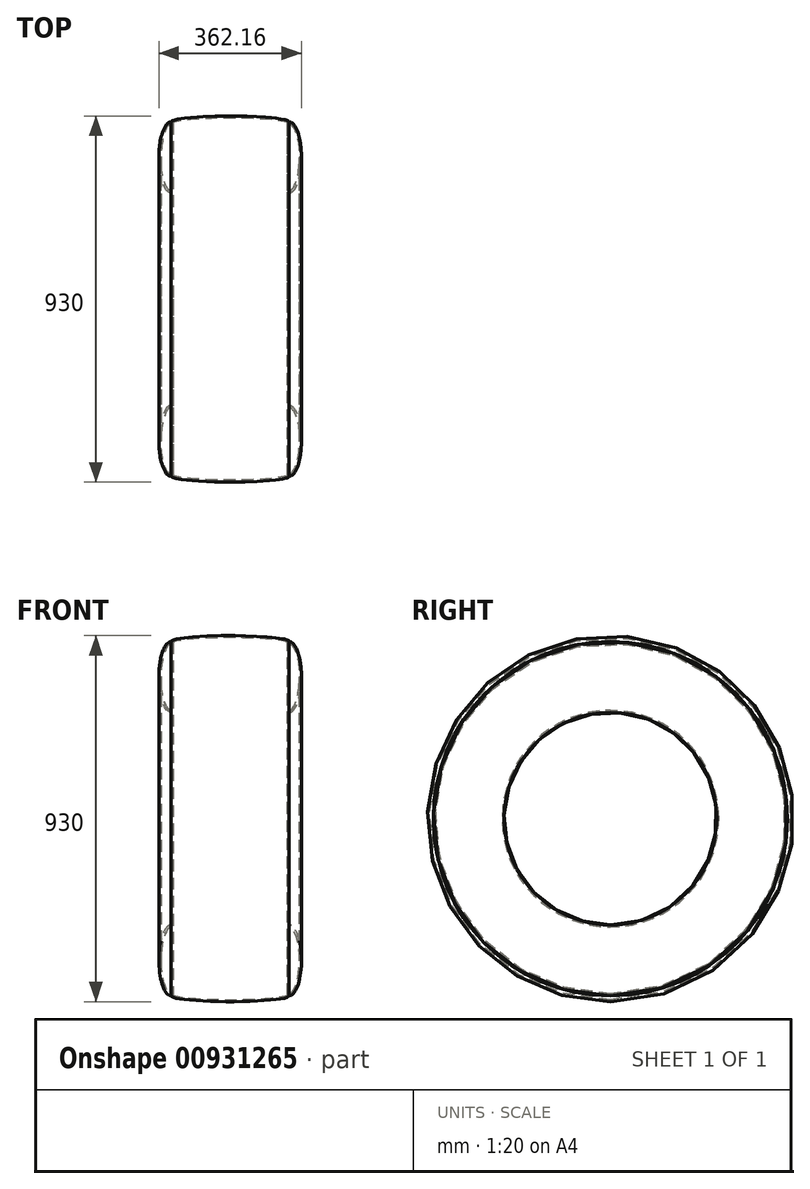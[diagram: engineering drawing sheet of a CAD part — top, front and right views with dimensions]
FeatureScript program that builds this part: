
annotation { "Feature Type Name" : "Feature", "Feature Type Description" : "" }
export const myFeature = defineFeature(function(context is Context, id is Id, definition is map)
    precondition{}
    {
        {
            var Q0;
            Q0=qCreatedBy(makeId("Top.planeOp"),FACE);
            var sketch = newSketch(context, id + "F0", { "sketchPlane" : qUnion([Q0])});
            skLineSegment(sketch, "E0", {"start": v(0, 0) * mm, "end": v(-385.6, 0) * mm, "construction": true});
            skLineSegment(sketch, "E1.bottom", {"start": v(-150, -270) * mm, "end": v(150, -270) * mm});
            skEllipticalArc(sketch, "E2", {});
            skEllipticalArc(sketch, "E3.MirrorCS", {});
            skEllipticalArc(sketch, "E4", {});
            skPoint(sketch, "E5.orphan", {"position": v(150, -450) * mm});
            const initialGuessF0  = {"E2": [-0.15, -0.36, 0, 1, 0.09, 0.03107780340244599, 0, 3.141592653589793], "E3.MirrorCS": [0.15, -0.36, 0, 1, 0.09, 0.03107780340244599, 3.141592653589793, 0], "E4": [0, -0.45, 1, 0, 0.15, 0.015, 3.141592653589793, 0]};
            skSetInitialGuess(sketch, initialGuessF0);
            skSolve(sketch);
        }
        {
            var Q0;
            Q0=makeQuery(id+"F0.imprint","IMPRINT",FACE,{"disambiguationData":[TD([[makeQuery(id+"F0.imprint","IMPRINT",EDGE,{"derivedFrom":sQuery(id+"F0.wireOp",EDGE,"E1.bottom")}),-1.0]])]});
            var Q1;
            Q1=sQuery(id+"F0.wireOp",EDGE,"E0");
            revolve(context, id + "F1", {"surfaceOperationType" : NewSurfaceOperationType.NEW, "entities" : qUnion([Q0]), "axis" : qUnion([Q1]), "revolveType" : RevolveType.FULL});
        }
        {
            var Q0;
            Q0=makeQuery(id+"F1.opRevolve","SWEPT_FACE",FACE,{"disambiguationData":[OSD([sQuery(id+"F0.wireOp",EDGE,"E1.bottom")])]});
            shell(context, id + "F2", {"entities" : qUnion([Q0]), "thickness" : 5 * mm});
        }
    });
